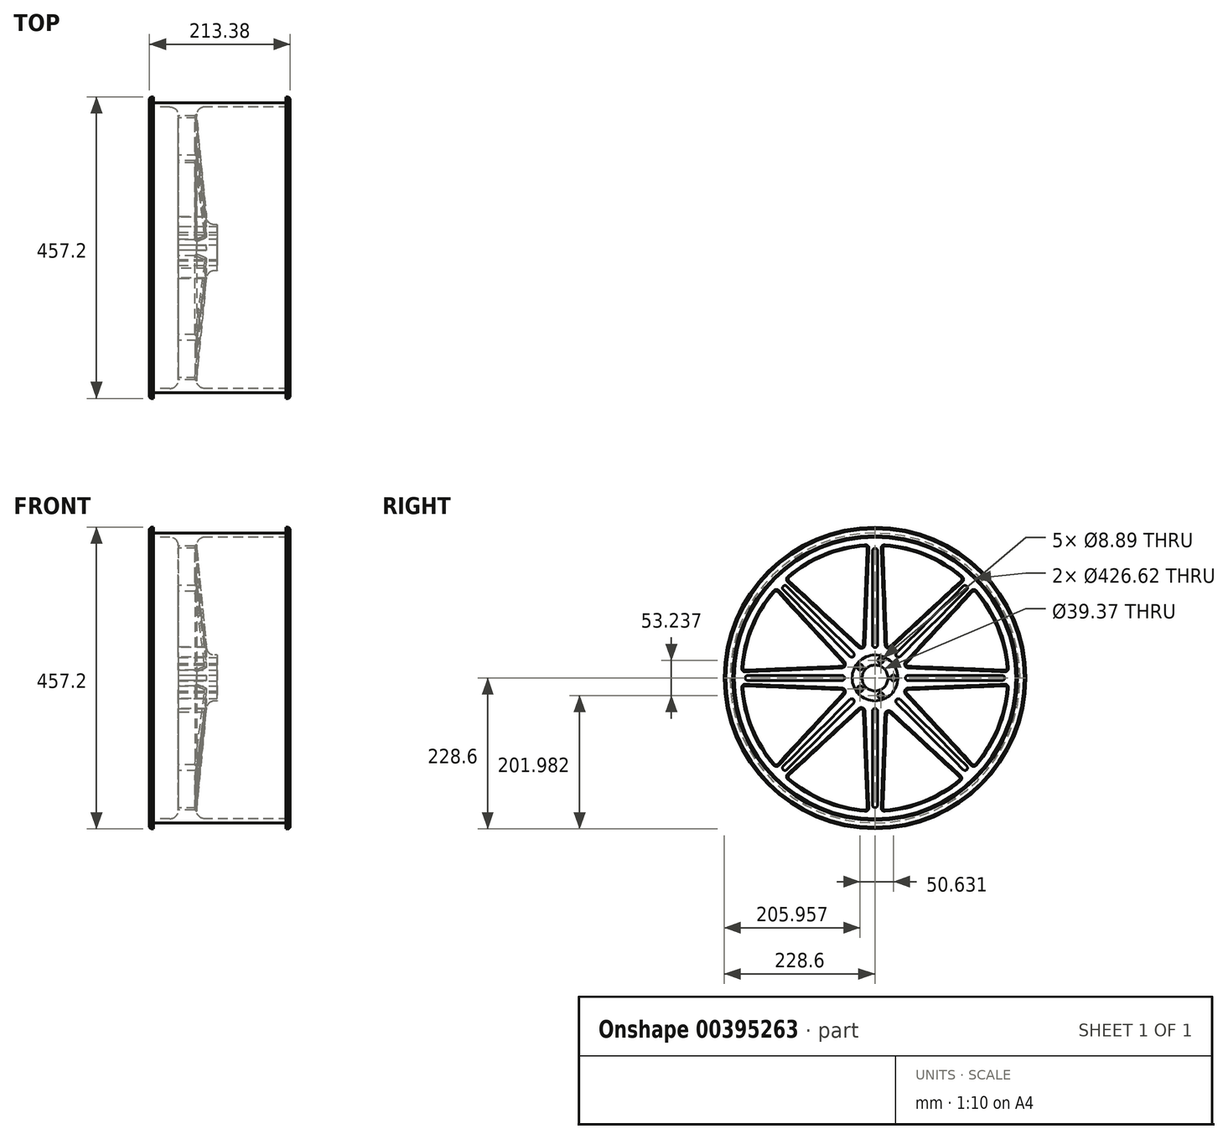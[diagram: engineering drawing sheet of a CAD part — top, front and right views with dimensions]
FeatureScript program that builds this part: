
annotation { "Feature Type Name" : "Feature", "Feature Type Description" : "" }
export const myFeature = defineFeature(function(context is Context, id is Id, definition is map)
    precondition{}
    {
        {
            var Q0;
            Q0=qCreatedBy(makeId("Top.planeOp"),FACE);
            var sketch = newSketch(context, id + "F0", { "sketchPlane" : qUnion([Q0])});
            skLineSegment(sketch, "E0", {"start": v(0, 0) * mm, "end": v(59.16, 0) * mm});
            skLineSegment(sketch, "E1", {"start": v(59.16, 0) * mm, "end": v(59.16, 34.73) * mm});
            skLineSegment(sketch, "E2", {"start": v(59.16, 34.73) * mm, "end": v(55.17, 34.73) * mm});
            skLineSegment(sketch, "E3", {"start": v(0, 0) * mm, "end": v(0, 200.61) * mm});
            skLineSegment(sketch, "E4", {"start": v(-12.7, 213.31) * mm, "end": v(-43.8, 213.31) * mm});
            skLineSegment(sketch, "E5", {"start": v(-43.8, 213.31) * mm, "end": v(-43.8, 228.6) * mm});
            skLineSegment(sketch, "E6", {"start": v(-43.8, 228.6) * mm, "end": v(-37.46, 228.6) * mm});
            skLineSegment(sketch, "E7", {"start": v(-37.46, 228.6) * mm, "end": v(-37.46, 219.66) * mm});
            skLineSegment(sketch, "E8", {"start": v(-37.46, 219.66) * mm, "end": v(163.22, 219.66) * mm});
            skLineSegment(sketch, "E9", {"start": v(163.22, 219.66) * mm, "end": v(163.22, 228.6) * mm});
            skLineSegment(sketch, "E10", {"start": v(163.22, 228.6) * mm, "end": v(169.57, 228.6) * mm});
            skLineSegment(sketch, "E11", {"start": v(169.57, 228.6) * mm, "end": v(169.57, 213.31) * mm});
            skLineSegment(sketch, "E12", {"start": v(169.57, 213.31) * mm, "end": v(40.14, 213.31) * mm});
            skLineSegment(sketch, "E13", {"start": v(27.5, 199.37) * mm, "end": v(42.53, 46.19) * mm});
            skPoint(sketch, "E14.visualSharp", {"position": v(26.13, 213.31) * mm});
            skArc(sketch, "E14.filletArc", {"start": v(40.14, 213.31) * mm, "mid": v(30.73, 209.14) * mm, "end": v(27.5, 199.37) * mm});
            skPoint(sketch, "E15.visualSharp", {"position": v(0, 213.31) * mm});
            skArc(sketch, "E15.filletArc", {"start": v(0, 200.61) * mm, "mid": v(-3.72, 209.6) * mm, "end": v(-12.7, 213.31) * mm});
            skPoint(sketch, "E16.visualSharp", {"position": v(43.65, 34.73) * mm});
            skArc(sketch, "E16.filletArc", {"start": v(42.53, 46.19) * mm, "mid": v(46.64, 38.02) * mm, "end": v(55.17, 34.73) * mm});
            skSolve(sketch);
        }
        {
            var Q0;
            Q0 = qSketchRegion(id + "F0", true);
            var Q1;
            Q1=sQuery(id+"F0.wireOp",EDGE,"E0");
            revolve(context, id + "F1", {"entities" : qUnion([Q0]), "axis" : qUnion([Q1]), "revolveType" : RevolveType.FULL});
        }
        {
            var Q0;
            Q0=makeQuery(id+"F1.opRevolve","SWEPT_FACE",FACE,{"disambiguationData":[OSD([sQuery(id+"F0.wireOp",EDGE,"E3")])]});
            var sketch = newSketch(context, id + "F2", { "sketchPlane" : qUnion([Q0])});
            skLineSegment(sketch, "E17", {"start": v(-11.95, 196.73) * mm, "end": v(-17.66, 50.17) * mm});
            skLineSegment(sketch, "E18.MirrorCS", {"start": v(11.95, 196.73) * mm, "end": v(17.66, 50.17) * mm});
            skLineSegment(sketch, "E19.1.0", {"start": v(-147.56, 130.66) * mm, "end": v(-47.96, 22.99) * mm});
            skLineSegment(sketch, "E19.1.2", {"start": v(-130.66, 147.56) * mm, "end": v(-22.99, 47.96) * mm});
            skLineSegment(sketch, "E19.2.0", {"start": v(-196.73, -11.95) * mm, "end": v(-50.17, -17.66) * mm});
            skLineSegment(sketch, "E19.2.2", {"start": v(-196.73, 11.95) * mm, "end": v(-50.17, 17.66) * mm});
            skLineSegment(sketch, "E19.3.0", {"start": v(-127.88, -149.9) * mm, "end": v(-22.85, -52.74) * mm});
            skLineSegment(sketch, "E19.3.2", {"start": v(-147.56, -130.66) * mm, "end": v(-47.96, -22.99) * mm});
            skLineSegment(sketch, "E19.4.0", {"start": v(11.95, -196.73) * mm, "end": v(17.66, -50.17) * mm});
            skLineSegment(sketch, "E19.4.2", {"start": v(-11.95, -196.73) * mm, "end": v(-17.52, -54.94) * mm});
            skLineSegment(sketch, "E19.5.0", {"start": v(147.56, -130.66) * mm, "end": v(47.96, -22.99) * mm});
            skLineSegment(sketch, "E19.5.2", {"start": v(130.66, -147.56) * mm, "end": v(22.99, -47.96) * mm});
            skLineSegment(sketch, "E19.6.0", {"start": v(196.73, 11.95) * mm, "end": v(50.17, 17.66) * mm});
            skLineSegment(sketch, "E19.6.2", {"start": v(196.73, -11.95) * mm, "end": v(50.17, -17.66) * mm});
            skLineSegment(sketch, "E19.7.0", {"start": v(130.66, 147.56) * mm, "end": v(22.99, 47.96) * mm});
            skLineSegment(sketch, "E19.7.2", {"start": v(147.56, 130.66) * mm, "end": v(47.96, 22.99) * mm});
            skArc(sketch, "E20", {"start": v(-15.37, 200.02) * mm, "mid": v(-76.77, 185.34) * mm, "end": v(-130.57, 152.3) * mm});
            skPoint(sketch, "E21.orphan", {"position": v(0, 200.61) * mm});
            skPoint(sketch, "E22.orphan", {"position": v(141.85, 141.85) * mm});
            skArc(sketch, "E23.trimOffspring", {"start": v(130.57, 152.3) * mm, "mid": v(76.77, 185.34) * mm, "end": v(15.37, 200.02) * mm});
            skPoint(sketch, "E24.orphan", {"position": v(200.61, 0) * mm});
            skPoint(sketch, "E25.orphan", {"position": v(141.85, -141.85) * mm});
            skPoint(sketch, "E26.orphan", {"position": v(0, -200.61) * mm});
            skPoint(sketch, "E27.orphan", {"position": v(-141.85, -141.85) * mm});
            skPoint(sketch, "E28.orphan", {"position": v(-200.61, 0) * mm});
            skPoint(sketch, "E29.orphan", {"position": v(-141.85, 141.85) * mm});
            skArc(sketch, "E30.trimOffspring", {"start": v(-200.02, -15.37) * mm, "mid": v(-185.34, -76.77) * mm, "end": v(-152.3, -130.57) * mm});
            skArc(sketch, "E31.trimOffspring", {"start": v(-152.3, 130.57) * mm, "mid": v(-185.34, 76.77) * mm, "end": v(-200.02, 15.37) * mm});
            skArc(sketch, "E32.trimOffspring", {"start": v(-127.75, -154.68) * mm, "mid": v(-75.07, -186.04) * mm, "end": v(-15.37, -200.02) * mm});
            skArc(sketch, "E33.trimOffspring", {"start": v(200.02, 15.37) * mm, "mid": v(185.34, 76.77) * mm, "end": v(152.3, 130.57) * mm});
            skArc(sketch, "E34.trimOffspring", {"start": v(152.3, -130.57) * mm, "mid": v(185.34, -76.77) * mm, "end": v(200.02, -15.37) * mm});
            skArc(sketch, "E35.trimOffspring", {"start": v(15.37, -200.02) * mm, "mid": v(76.77, -185.34) * mm, "end": v(130.57, -152.3) * mm});
            skPoint(sketch, "E36.visualSharp", {"position": v(-130.53, -152.34) * mm});
            skArc(sketch, "E36.filletArc", {"start": v(-127.88, -149.9) * mm, "mid": v(-128.9, -152.32) * mm, "end": v(-127.75, -154.68) * mm});
            skPoint(sketch, "E37.visualSharp", {"position": v(-149.96, -133.25) * mm});
            skArc(sketch, "E37.filletArc", {"start": v(-152.3, -130.57) * mm, "mid": v(-149.95, -131.68) * mm, "end": v(-147.56, -130.66) * mm});
            skPoint(sketch, "E38.visualSharp", {"position": v(-200.26, -11.82) * mm});
            skArc(sketch, "E38.filletArc", {"start": v(-196.73, -11.95) * mm, "mid": v(-199.14, -12.92) * mm, "end": v(-200.02, -15.37) * mm});
            skPoint(sketch, "E39.visualSharp", {"position": v(-200.26, 11.82) * mm});
            skArc(sketch, "E39.filletArc", {"start": v(-200.02, 15.37) * mm, "mid": v(-199.14, 12.92) * mm, "end": v(-196.73, 11.95) * mm});
            skPoint(sketch, "E40.visualSharp", {"position": v(-149.96, 133.25) * mm});
            skArc(sketch, "E40.filletArc", {"start": v(-147.56, 130.66) * mm, "mid": v(-149.95, 131.68) * mm, "end": v(-152.3, 130.57) * mm});
            skPoint(sketch, "E41.visualSharp", {"position": v(-133.25, 149.96) * mm});
            skArc(sketch, "E41.filletArc", {"start": v(-130.57, 152.3) * mm, "mid": v(-131.68, 149.95) * mm, "end": v(-130.66, 147.56) * mm});
            skPoint(sketch, "E42.visualSharp", {"position": v(-11.82, -200.26) * mm});
            skArc(sketch, "E42.filletArc", {"start": v(-15.37, -200.02) * mm, "mid": v(-12.92, -199.14) * mm, "end": v(-11.95, -196.73) * mm});
            skPoint(sketch, "E43.visualSharp", {"position": v(11.82, -200.26) * mm});
            skArc(sketch, "E43.filletArc", {"start": v(11.95, -196.73) * mm, "mid": v(12.92, -199.14) * mm, "end": v(15.37, -200.02) * mm});
            skPoint(sketch, "E44.visualSharp", {"position": v(133.25, -149.96) * mm});
            skArc(sketch, "E44.filletArc", {"start": v(130.57, -152.3) * mm, "mid": v(131.68, -149.95) * mm, "end": v(130.66, -147.56) * mm});
            skPoint(sketch, "E45.visualSharp", {"position": v(149.96, -133.25) * mm});
            skArc(sketch, "E45.filletArc", {"start": v(147.56, -130.66) * mm, "mid": v(149.95, -131.68) * mm, "end": v(152.3, -130.57) * mm});
            skPoint(sketch, "E46.visualSharp", {"position": v(200.26, -11.82) * mm});
            skArc(sketch, "E46.filletArc", {"start": v(200.02, -15.37) * mm, "mid": v(199.14, -12.92) * mm, "end": v(196.73, -11.95) * mm});
            skPoint(sketch, "E47.visualSharp", {"position": v(200.26, 11.82) * mm});
            skArc(sketch, "E47.filletArc", {"start": v(196.73, 11.95) * mm, "mid": v(199.14, 12.92) * mm, "end": v(200.02, 15.37) * mm});
            skPoint(sketch, "E48.visualSharp", {"position": v(149.96, 133.25) * mm});
            skArc(sketch, "E48.filletArc", {"start": v(152.3, 130.57) * mm, "mid": v(149.95, 131.68) * mm, "end": v(147.56, 130.66) * mm});
            skPoint(sketch, "E49.visualSharp", {"position": v(133.25, 149.96) * mm});
            skArc(sketch, "E49.filletArc", {"start": v(130.66, 147.56) * mm, "mid": v(131.68, 149.95) * mm, "end": v(130.57, 152.3) * mm});
            skPoint(sketch, "E50.visualSharp", {"position": v(11.82, 200.26) * mm});
            skArc(sketch, "E50.filletArc", {"start": v(15.37, 200.02) * mm, "mid": v(12.92, 199.14) * mm, "end": v(11.95, 196.73) * mm});
            skPoint(sketch, "E51.visualSharp", {"position": v(-11.82, 200.26) * mm});
            skArc(sketch, "E51.filletArc", {"start": v(-11.95, 196.73) * mm, "mid": v(-12.92, 199.14) * mm, "end": v(-15.37, 200.02) * mm});
            skPoint(sketch, "E52.visualSharp", {"position": v(-17.93, 43.28) * mm});
            skArc(sketch, "E52.filletArc", {"start": v(-22.99, 47.96) * mm, "mid": v(-19.62, 47.36) * mm, "end": v(-17.66, 50.17) * mm});
            skPoint(sketch, "E53.visualSharp", {"position": v(-43.28, 17.93) * mm});
            skArc(sketch, "E53.filletArc", {"start": v(-50.17, 17.66) * mm, "mid": v(-47.36, 19.62) * mm, "end": v(-47.96, 22.99) * mm});
            skPoint(sketch, "E54.visualSharp", {"position": v(-43.28, -17.93) * mm});
            skArc(sketch, "E54.filletArc", {"start": v(-47.96, -22.99) * mm, "mid": v(-47.36, -19.62) * mm, "end": v(-50.17, -17.66) * mm});
            skPoint(sketch, "E55.visualSharp", {"position": v(-17.8, -48.06) * mm});
            skArc(sketch, "E55.filletArc", {"start": v(-17.52, -54.94) * mm, "mid": v(-19.48, -52.13) * mm, "end": v(-22.85, -52.74) * mm});
            skPoint(sketch, "E56.visualSharp", {"position": v(17.93, -43.28) * mm});
            skArc(sketch, "E56.filletArc", {"start": v(22.99, -47.96) * mm, "mid": v(19.62, -47.36) * mm, "end": v(17.66, -50.17) * mm});
            skPoint(sketch, "E57.visualSharp", {"position": v(43.28, -17.93) * mm});
            skArc(sketch, "E57.filletArc", {"start": v(50.17, -17.66) * mm, "mid": v(47.36, -19.62) * mm, "end": v(47.96, -22.99) * mm});
            skPoint(sketch, "E58.visualSharp", {"position": v(43.28, 17.93) * mm});
            skArc(sketch, "E58.filletArc", {"start": v(47.96, 22.99) * mm, "mid": v(47.36, 19.62) * mm, "end": v(50.17, 17.66) * mm});
            skPoint(sketch, "E59.visualSharp", {"position": v(17.93, 43.28) * mm});
            skArc(sketch, "E59.filletArc", {"start": v(17.66, 50.17) * mm, "mid": v(19.62, 47.36) * mm, "end": v(22.99, 47.96) * mm});
            skSolve(sketch);
        }
        {
            var Q0;
            Q0 = qSketchRegion(id + "F2", true);
            extrude(context, id + "F3", {"entities" : qUnion([Q0]), "operationType" : NewBodyOperationType.REMOVE, "endBound" : BoundingType.THROUGH_ALL, "oppositeDirection" : true, "depth" : 25.4 * mm});
        }
        {
            var Q0;
            Q0=makeQuery(id+"F1.opRevolve","SWEPT_FACE",FACE,{"disambiguationData":[OSD([sQuery(id+"F0.wireOp",EDGE,"E1")])]});
            var sketch = newSketch(context, id + "F4", { "sketchPlane" : qUnion([Q0])});
            skCircle(sketch, "E60", {"center": v(27.99, 0) * mm, "radius": 1.48 * mm});
            skCircle(sketch, "E61.1.0", {"center": v(8.65, 26.62) * mm, "radius": 1.48 * mm});
            skCircle(sketch, "E61.2.0", {"center": v(-22.64, 16.45) * mm, "radius": 1.48 * mm});
            skCircle(sketch, "E61.3.0", {"center": v(-22.64, -16.45) * mm, "radius": 1.48 * mm});
            skCircle(sketch, "E61.4.0", {"center": v(8.65, -26.62) * mm, "radius": 1.48 * mm});
            skPoint(sketch, "E61.center", {"position": v(0, 0) * mm});
            skCircle(sketch, "E62", {"center": v(0, 0) * mm, "radius": 14.4 * mm});
            skCircle(sketch, "E63", {"center": v(0, 0) * mm, "radius": 11.34 * mm});
            skSolve(sketch);
        }
        {
            var Q0;
            Q0=sQuery(id+"F4.wireOp",VERTEX,"E61.1.0.center");
            var Q1;
            Q1=sQuery(id+"F4.wireOp",VERTEX,"E60.center");
            var Q2;
            Q2=sQuery(id+"F4.wireOp",VERTEX,"E61.4.0.center");
            var Q3;
            Q3=sQuery(id+"F4.wireOp",VERTEX,"E61.3.0.center");
            var Q4;
            Q4=sQuery(id+"F4.wireOp",VERTEX,"E61.2.0.center");
            var Q5;
            Q5=makeQuery(id+"F1.opRevolve","SWEPT_BODY",BODY,{"disambiguationData":[OSD([sQuery(id+"F0.wireOp",EDGE,"E0"),sQuery(id+"F0.wireOp",EDGE,"E1"),sQuery(id+"F0.wireOp",EDGE,"E2"),sQuery(id+"F0.wireOp",EDGE,"E3"),sQuery(id+"F0.wireOp",EDGE,"E4"),sQuery(id+"F0.wireOp",EDGE,"E5"),sQuery(id+"F0.wireOp",EDGE,"E6"),sQuery(id+"F0.wireOp",EDGE,"E7"),sQuery(id+"F0.wireOp",EDGE,"E8"),sQuery(id+"F0.wireOp",EDGE,"E9"),sQuery(id+"F0.wireOp",EDGE,"E10"),sQuery(id+"F0.wireOp",EDGE,"E11"),sQuery(id+"F0.wireOp",EDGE,"E12"),sQuery(id+"F0.wireOp",EDGE,"E13"),sQuery(id+"F0.wireOp",EDGE,"E14.filletArc"),sQuery(id+"F0.wireOp",EDGE,"E15.filletArc"),sQuery(id+"F0.wireOp",EDGE,"E16.filletArc")])]});
            hole(context, id + "F5", {"style" : HoleStyle.SIMPLE, "endStyle" : HoleEndStyle.THROUGH, "holeDiameter" : 8.9 * mm, "isTappedThrough" : true, "tappedDepth" : 12.7 * mm, "tapClearance" : 3, "locations" : qUnion([Q0, Q1, Q2, Q3, Q4]), "scope" : qUnion([Q5])});
        }
        {
            var Q0;
            Q0=sQuery(id+"F4.wireOp",VERTEX,"E61.center");
            var Q1;
            Q1=makeQuery(id+"F1.opRevolve","SWEPT_BODY",BODY,{"disambiguationData":[OSD([sQuery(id+"F0.wireOp",EDGE,"E0"),sQuery(id+"F0.wireOp",EDGE,"E1"),sQuery(id+"F0.wireOp",EDGE,"E2"),sQuery(id+"F0.wireOp",EDGE,"E3"),sQuery(id+"F0.wireOp",EDGE,"E4"),sQuery(id+"F0.wireOp",EDGE,"E5"),sQuery(id+"F0.wireOp",EDGE,"E6"),sQuery(id+"F0.wireOp",EDGE,"E7"),sQuery(id+"F0.wireOp",EDGE,"E8"),sQuery(id+"F0.wireOp",EDGE,"E9"),sQuery(id+"F0.wireOp",EDGE,"E10"),sQuery(id+"F0.wireOp",EDGE,"E11"),sQuery(id+"F0.wireOp",EDGE,"E12"),sQuery(id+"F0.wireOp",EDGE,"E13"),sQuery(id+"F0.wireOp",EDGE,"E14.filletArc"),sQuery(id+"F0.wireOp",EDGE,"E15.filletArc"),sQuery(id+"F0.wireOp",EDGE,"E16.filletArc")])]});
            hole(context, id + "F6", {"style" : HoleStyle.SIMPLE, "endStyle" : HoleEndStyle.THROUGH, "holeDiameter" : 39.37 * mm, "isTappedThrough" : true, "tappedDepth" : 12.7 * mm, "tapClearance" : 3, "locations" : qUnion([Q0]), "scope" : qUnion([Q1])});
        }
        {
            var Q0;
            Q0=makeQuery(id+"F2.imprint","IMPRINT",FACE,{"disambiguationData":[TD([[makeQuery(id+"F2.imprint","IMPRINT",EDGE,{"derivedFrom":sQuery(id+"F2.wireOp",EDGE,"E17")}),1.0]])]});
            var sketch = newSketch(context, id + "F7", { "sketchPlane" : qUnion([Q0])});
            skLineSegment(sketch, "E64.0", {"start": v(3.8, 49.91) * mm, "end": v(3.8, 192.83) * mm});
            skLineSegment(sketch, "E65.0", {"start": v(-3.81, 49.91) * mm, "end": v(-3.81, 192.83) * mm});
            skArc(sketch, "E66", {"start": v(3.8, 192.83) * mm, "mid": v(0, 196.64) * mm, "end": v(-3.81, 192.83) * mm});
            skArc(sketch, "E67", {"start": v(-3.81, 49.91) * mm, "mid": v(0, 46.1) * mm, "end": v(3.8, 49.91) * mm});
            skLineSegment(sketch, "E68.1.0", {"start": v(-32.6, 37.99) * mm, "end": v(-133.66, 139.05) * mm});
            skLineSegment(sketch, "E68.1.1", {"start": v(-37.99, 32.6) * mm, "end": v(-139.05, 133.66) * mm});
            skArc(sketch, "E68.1.2", {"start": v(-133.66, 139.05) * mm, "mid": v(-139.05, 139.05) * mm, "end": v(-139.05, 133.66) * mm});
            skArc(sketch, "E68.1.3", {"start": v(-37.99, 32.6) * mm, "mid": v(-32.6, 32.6) * mm, "end": v(-32.6, 37.99) * mm});
            skLineSegment(sketch, "E68.2.0", {"start": v(-49.91, 3.8) * mm, "end": v(-192.83, 3.8) * mm});
            skLineSegment(sketch, "E68.2.1", {"start": v(-49.91, -3.81) * mm, "end": v(-192.83, -3.81) * mm});
            skArc(sketch, "E68.2.2", {"start": v(-192.83, 3.8) * mm, "mid": v(-196.64, 0) * mm, "end": v(-192.83, -3.81) * mm});
            skArc(sketch, "E68.2.3", {"start": v(-49.91, -3.81) * mm, "mid": v(-46.1, 0) * mm, "end": v(-49.91, 3.8) * mm});
            skPoint(sketch, "E68.center", {"position": v(0, 0) * mm});
            skLineSegment(sketch, "E69.1.3.0", {"start": v(-37.99, -32.6) * mm, "end": v(-139.05, -133.66) * mm});
            skLineSegment(sketch, "E69.3.3.0", {"start": v(-32.6, -37.99) * mm, "end": v(-133.66, -139.05) * mm});
            skArc(sketch, "E69.6.3.0", {"start": v(-139.05, -133.66) * mm, "mid": v(-139.05, -139.05) * mm, "end": v(-133.66, -139.05) * mm});
            skArc(sketch, "E69.10.3.0", {"start": v(-32.6, -37.99) * mm, "mid": v(-32.6, -32.6) * mm, "end": v(-37.99, -32.6) * mm});
            skLineSegment(sketch, "E70.1.4.0", {"start": v(-3.8, -49.91) * mm, "end": v(-3.81, -192.83) * mm});
            skLineSegment(sketch, "E70.3.4.0", {"start": v(3.81, -49.91) * mm, "end": v(3.8, -192.83) * mm});
            skArc(sketch, "E70.6.4.0", {"start": v(-3.8, -192.83) * mm, "mid": v(0, -196.64) * mm, "end": v(3.81, -192.83) * mm});
            skArc(sketch, "E70.10.4.0", {"start": v(3.8, -49.91) * mm, "mid": v(0, -46.1) * mm, "end": v(-3.8, -49.91) * mm});
            skLineSegment(sketch, "E71.1.5.0", {"start": v(32.6, -37.99) * mm, "end": v(133.66, -139.05) * mm});
            skLineSegment(sketch, "E71.3.5.0", {"start": v(37.99, -32.6) * mm, "end": v(139.05, -133.66) * mm});
            skArc(sketch, "E71.6.5.0", {"start": v(133.66, -139.05) * mm, "mid": v(139.05, -139.05) * mm, "end": v(139.05, -133.66) * mm});
            skArc(sketch, "E71.10.5.0", {"start": v(37.99, -32.6) * mm, "mid": v(32.6, -32.6) * mm, "end": v(32.6, -37.99) * mm});
            skLineSegment(sketch, "E72.1.6.0", {"start": v(49.91, -3.8) * mm, "end": v(192.83, -3.81) * mm});
            skLineSegment(sketch, "E72.3.6.0", {"start": v(49.91, 3.81) * mm, "end": v(192.83, 3.8) * mm});
            skArc(sketch, "E72.6.6.0", {"start": v(192.83, -3.81) * mm, "mid": v(196.64, 0) * mm, "end": v(192.83, 3.8) * mm});
            skArc(sketch, "E72.10.6.0", {"start": v(49.91, 3.8) * mm, "mid": v(46.1, 0) * mm, "end": v(49.91, -3.8) * mm});
            skLineSegment(sketch, "E73.1.7.0", {"start": v(37.99, 32.6) * mm, "end": v(139.05, 133.66) * mm});
            skLineSegment(sketch, "E73.3.7.0", {"start": v(32.6, 37.99) * mm, "end": v(133.66, 139.05) * mm});
            skArc(sketch, "E73.6.7.0", {"start": v(139.05, 133.66) * mm, "mid": v(139.05, 139.05) * mm, "end": v(133.66, 139.05) * mm});
            skArc(sketch, "E73.10.7.0", {"start": v(32.6, 37.99) * mm, "mid": v(32.6, 32.6) * mm, "end": v(37.99, 32.6) * mm});
            skSolve(sketch);
        }
        {
            var Q0;
            Q0 = qSketchRegion(id + "F7", true);
            extrude(context, id + "F8", {"entities" : qUnion([Q0]), "operationType" : NewBodyOperationType.REMOVE, "endBound" : BoundingType.THROUGH_ALL, "oppositeDirection" : true, "depth" : 25.4 * mm});
        }
        {
            var Q0;
            Q0=makeQuery(id+"F5.hole-3.boolean.opBoolean","INTERSECT",EDGE,{"derivedFrom":[makeQuery(id+"F1.opRevolve","SWEPT_FACE",FACE,{"disambiguationData":[OSD([sQuery(id+"F0.wireOp",EDGE,"E3")])]}),makeQuery(id+"F5.hole-3.opRevolve","SWEPT_FACE",FACE,{"disambiguationData":[OSD([sQuery(id+"F5.hole-3.sketch.wireOp",EDGE,"core_line_2")])]})]});
            var Q1;
            Q1=makeQuery(id+"F5.hole-4.boolean.opBoolean","INTERSECT",EDGE,{"derivedFrom":[makeQuery(id+"F1.opRevolve","SWEPT_FACE",FACE,{"disambiguationData":[OSD([sQuery(id+"F0.wireOp",EDGE,"E3")])]}),makeQuery(id+"F5.hole-4.opRevolve","SWEPT_FACE",FACE,{"disambiguationData":[OSD([sQuery(id+"F5.hole-4.sketch.wireOp",EDGE,"core_line_2")])]})]});
            var Q2;
            Q2=makeQuery(id+"F5.hole-0.boolean.opBoolean","INTERSECT",EDGE,{"derivedFrom":[makeQuery(id+"F1.opRevolve","SWEPT_FACE",FACE,{"disambiguationData":[OSD([sQuery(id+"F0.wireOp",EDGE,"E3")])]}),makeQuery(id+"F5.hole-0.opRevolve","SWEPT_FACE",FACE,{"disambiguationData":[OSD([sQuery(id+"F5.hole-0.sketch.wireOp",EDGE,"core_line_2")])]})]});
            var Q3;
            Q3=makeQuery(id+"F5.hole-1.boolean.opBoolean","INTERSECT",EDGE,{"derivedFrom":[makeQuery(id+"F1.opRevolve","SWEPT_FACE",FACE,{"disambiguationData":[OSD([sQuery(id+"F0.wireOp",EDGE,"E3")])]}),makeQuery(id+"F5.hole-1.opRevolve","SWEPT_FACE",FACE,{"disambiguationData":[OSD([sQuery(id+"F5.hole-1.sketch.wireOp",EDGE,"core_line_2")])]})]});
            var Q4;
            Q4=makeQuery(id+"F5.hole-2.boolean.opBoolean","INTERSECT",EDGE,{"derivedFrom":[makeQuery(id+"F1.opRevolve","SWEPT_FACE",FACE,{"disambiguationData":[OSD([sQuery(id+"F0.wireOp",EDGE,"E3")])]}),makeQuery(id+"F5.hole-2.opRevolve","SWEPT_FACE",FACE,{"disambiguationData":[OSD([sQuery(id+"F5.hole-2.sketch.wireOp",EDGE,"core_line_2")])]})]});
            var Q5;
            Q5=makeQuery(id+"F1.opRevolve","SWEPT_EDGE",EDGE,{"disambiguationData":[OSD([sQuery(id+"F0.wireOp",EDGE,"E4"),sQuery(id+"F0.wireOp",EDGE,"E5")])]});
            var Q6;
            Q6=makeQuery(id+"F3.boolean.opBoolean","COPY",EDGE,{"derivedFrom":makeQuery(id+"F3.opExtrude","CAP_EDGE",EDGE,{"disambiguationData":[OSD([sQuery(id+"F2.wireOp",EDGE,"E19.3.2")])],"isStart":true})});
            var Q7;
            Q7=makeQuery(id+"F3.boolean.opBoolean","COPY",EDGE,{"derivedFrom":makeQuery(id+"F3.opExtrude","CAP_EDGE",EDGE,{"disambiguationData":[OSD([sQuery(id+"F2.wireOp",EDGE,"E19.3.0")])],"isStart":true})});
            var Q8;
            Q8=makeQuery(id+"F3.boolean.opBoolean","COPY",EDGE,{"derivedFrom":makeQuery(id+"F3.opExtrude","CAP_EDGE",EDGE,{"disambiguationData":[OSD([sQuery(id+"F2.wireOp",EDGE,"E19.2.2")])],"isStart":true})});
            var Q9;
            Q9=makeQuery(id+"F3.boolean.opBoolean","COPY",EDGE,{"derivedFrom":makeQuery(id+"F3.opExtrude","CAP_EDGE",EDGE,{"disambiguationData":[OSD([sQuery(id+"F2.wireOp",EDGE,"E19.1.2")])],"isStart":true})});
            var Q10;
            Q10=makeQuery(id+"F3.boolean.opBoolean","COPY",EDGE,{"derivedFrom":makeQuery(id+"F3.opExtrude","CAP_EDGE",EDGE,{"disambiguationData":[OSD([sQuery(id+"F2.wireOp",EDGE,"E18.MirrorCS")])],"isStart":true})});
            var Q11;
            Q11=makeQuery(id+"F3.boolean.opBoolean","COPY",EDGE,{"derivedFrom":makeQuery(id+"F3.opExtrude","CAP_EDGE",EDGE,{"disambiguationData":[OSD([sQuery(id+"F2.wireOp",EDGE,"E19.6.0")])],"isStart":true})});
            var Q12;
            Q12=makeQuery(id+"F3.boolean.opBoolean","COPY",EDGE,{"derivedFrom":makeQuery(id+"F3.opExtrude","CAP_EDGE",EDGE,{"disambiguationData":[OSD([sQuery(id+"F2.wireOp",EDGE,"E19.6.2")])],"isStart":true})});
            var Q13;
            Q13=makeQuery(id+"F3.boolean.opBoolean","COPY",EDGE,{"derivedFrom":makeQuery(id+"F3.opExtrude","CAP_EDGE",EDGE,{"disambiguationData":[OSD([sQuery(id+"F2.wireOp",EDGE,"E19.5.2")])],"isStart":true})});
            var Q14;
            Q14=makeQuery(id+"F1.opRevolve","SWEPT_EDGE",EDGE,{"disambiguationData":[OSD([sQuery(id+"F0.wireOp",EDGE,"E11"),sQuery(id+"F0.wireOp",EDGE,"E12")])]});
            var Q15;
            Q15=makeQuery(id+"F1.opRevolve","SWEPT_EDGE",EDGE,{"disambiguationData":[OSD([sQuery(id+"F0.wireOp",EDGE,"E10"),sQuery(id+"F0.wireOp",EDGE,"E11")])]});
            var Q16;
            Q16=makeQuery(id+"F1.opRevolve","SWEPT_EDGE",EDGE,{"disambiguationData":[OSD([sQuery(id+"F0.wireOp",EDGE,"E5"),sQuery(id+"F0.wireOp",EDGE,"E6")])]});
            var Q17;
            Q17=makeQuery(id+"F3.boolean.opBoolean","INTERSECT",EDGE,{"derivedFrom":[makeQuery(id+"F1.opRevolve","SWEPT_FACE",FACE,{"disambiguationData":[OSD([sQuery(id+"F0.wireOp",EDGE,"E14.filletArc")])]}),makeQuery(id+"F3.opExtrude","SWEPT_FACE",FACE,{"disambiguationData":[OSD([sQuery(id+"F2.wireOp",EDGE,"E20")])]})]});
            var Q18;
            Q18=makeQuery(id+"F3.boolean.opBoolean","INTERSECT",EDGE,{"derivedFrom":[makeQuery(id+"F1.opRevolve","SWEPT_FACE",FACE,{"disambiguationData":[OSD([sQuery(id+"F0.wireOp",EDGE,"E14.filletArc")])]}),makeQuery(id+"F3.opExtrude","SWEPT_FACE",FACE,{"disambiguationData":[OSD([sQuery(id+"F2.wireOp",EDGE,"E23.trimOffspring")])]})]});
            var Q19;
            Q19=makeQuery(id+"F3.boolean.opBoolean","INTERSECT",EDGE,{"derivedFrom":[makeQuery(id+"F1.opRevolve","SWEPT_FACE",FACE,{"disambiguationData":[OSD([sQuery(id+"F0.wireOp",EDGE,"E13")])]}),makeQuery(id+"F3.opExtrude","SWEPT_FACE",FACE,{"disambiguationData":[OSD([sQuery(id+"F2.wireOp",EDGE,"E19.7.2")])]})]});
            var Q20;
            Q20=makeQuery(id+"F3.boolean.opBoolean","INTERSECT",EDGE,{"derivedFrom":[makeQuery(id+"F1.opRevolve","SWEPT_FACE",FACE,{"disambiguationData":[OSD([sQuery(id+"F0.wireOp",EDGE,"E13")])]}),makeQuery(id+"F3.opExtrude","SWEPT_FACE",FACE,{"disambiguationData":[OSD([sQuery(id+"F2.wireOp",EDGE,"E19.6.2")])]})]});
            var Q21;
            Q21=makeQuery(id+"F3.boolean.opBoolean","INTERSECT",EDGE,{"derivedFrom":[makeQuery(id+"F1.opRevolve","SWEPT_FACE",FACE,{"disambiguationData":[OSD([sQuery(id+"F0.wireOp",EDGE,"E13")])]}),makeQuery(id+"F3.opExtrude","SWEPT_FACE",FACE,{"disambiguationData":[OSD([sQuery(id+"F2.wireOp",EDGE,"E19.4.0")])]})]});
            var Q22;
            Q22=makeQuery(id+"F3.boolean.opBoolean","INTERSECT",EDGE,{"derivedFrom":[makeQuery(id+"F1.opRevolve","SWEPT_FACE",FACE,{"disambiguationData":[OSD([sQuery(id+"F0.wireOp",EDGE,"E13")])]}),makeQuery(id+"F3.opExtrude","SWEPT_FACE",FACE,{"disambiguationData":[OSD([sQuery(id+"F2.wireOp",EDGE,"E19.4.2")])]})]});
            var Q23;
            Q23=makeQuery(id+"F3.boolean.opBoolean","INTERSECT",EDGE,{"derivedFrom":[makeQuery(id+"F1.opRevolve","SWEPT_FACE",FACE,{"disambiguationData":[OSD([sQuery(id+"F0.wireOp",EDGE,"E13")])]}),makeQuery(id+"F3.opExtrude","SWEPT_FACE",FACE,{"disambiguationData":[OSD([sQuery(id+"F2.wireOp",EDGE,"E19.3.2")])]})]});
            var Q24;
            Q24=makeQuery(id+"F3.boolean.opBoolean","INTERSECT",EDGE,{"derivedFrom":[makeQuery(id+"F1.opRevolve","SWEPT_FACE",FACE,{"disambiguationData":[OSD([sQuery(id+"F0.wireOp",EDGE,"E13")])]}),makeQuery(id+"F3.opExtrude","SWEPT_FACE",FACE,{"disambiguationData":[OSD([sQuery(id+"F2.wireOp",EDGE,"E19.2.2")])]})]});
            var Q25;
            Q25=makeQuery(id+"F6.hole-0.boolean.opBoolean","COPY",EDGE,{"derivedFrom":makeQuery(id+"F6.hole-0.opRevolve","SWEPT_EDGE",EDGE,{"disambiguationData":[OSD([sQuery(id+"F6.hole-0.sketch.wireOp",EDGE,"core_line_2"),sQuery(id+"F6.hole-0.sketch.wireOp",EDGE,"core_line_3")])]})});
            chamfer(context, id + "F9", {"entities" : qUnion([Q0, Q1, Q2, Q3, Q4, Q5, Q6, Q7, Q8, Q9, Q10, Q11, Q12, Q13, Q14, Q15, Q16, Q17, Q18, Q19, Q20, Q21, Q22, Q23, Q24, Q25]), "width" : 2.54 * mm, "tangentPropagation" : true});
        }
    });
